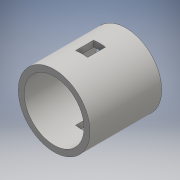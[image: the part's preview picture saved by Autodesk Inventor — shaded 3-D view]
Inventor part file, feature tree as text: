
AUTODESK INVENTOR PART (.ipt)
format: ipt  version: 2016 (Build 200138000, 138)  size: 111,104 bytes
history: native  units: mm
features: extrude x2, sketch x2, other x1
ambient origin geometry x8: Origin, YZ Plane, XZ Plane, XY Plane, X Axis, Y Axis, Z Axis, Center Point
bodies: Body1 (feature_tree)
feature tree (5):
  other  "ソリッド1"
  extrude  "押し出し1"  Depth=50.0mm
  extrude  "押し出し2"  Depth=60.0mm
  sketch  "スケッチ1"
  sketch  "スケッチ2"
